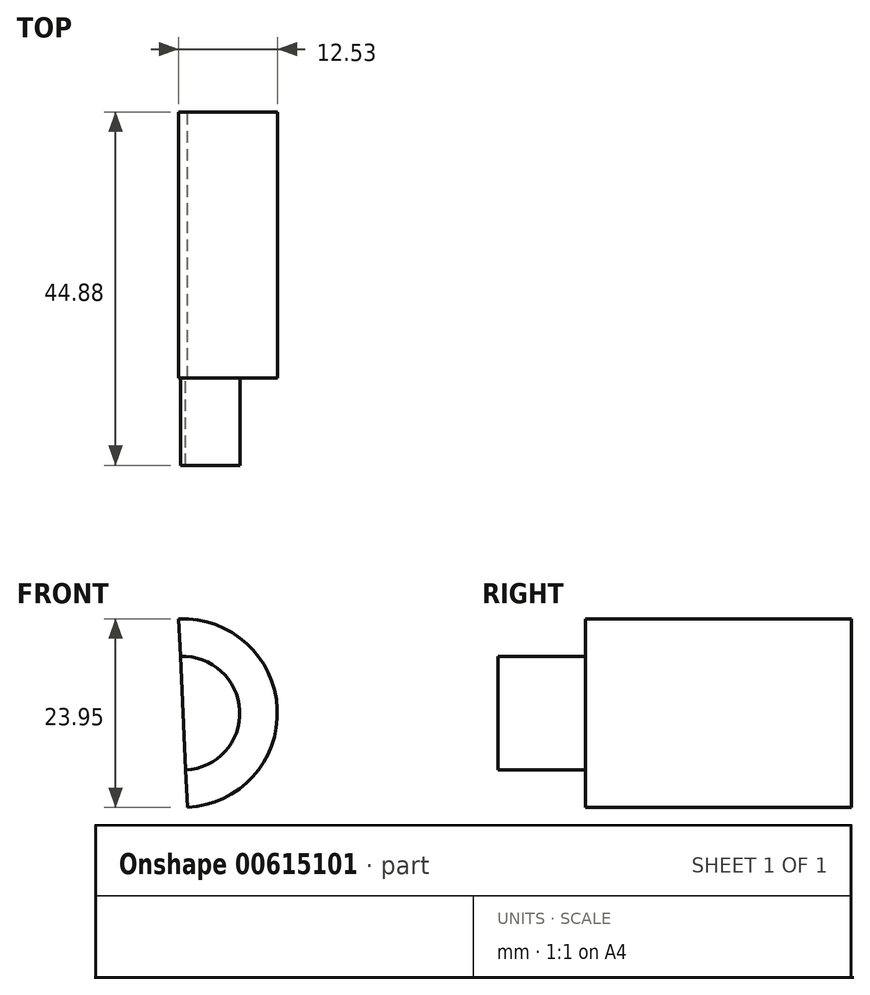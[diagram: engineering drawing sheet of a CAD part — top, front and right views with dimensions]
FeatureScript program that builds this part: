
annotation { "Feature Type Name" : "Feature", "Feature Type Description" : "" }
export const myFeature = defineFeature(function(context is Context, id is Id, definition is map)
    precondition{}
    {
        {
            var Q0;
            Q0=qCreatedBy(makeId("Front.planeOp"),FACE);
            var sketch = newSketch(context, id + "F0", { "sketchPlane" : qUnion([Q0])});
            skArc(sketch, "E0", {"start": v(-59.33, 43.04) * mm, "mid": v(-47.9, 55.56) * mm, "end": v(-60.43, 66.98) * mm});
            skLineSegment(sketch, "E1", {"start": v(-60.43, 66.98) * mm, "end": v(-59.33, 43.04) * mm});
            skSolve(sketch);
        }
        {
            var Q0;
            Q0 = qSketchRegion(id + "F0", true);
            extrude(context, id + "F1", {"entities" : qUnion([Q0]), "depth" : 33.78 * mm, "offsetDistance" : 25.4 * mm});
        }
        {
            var Q0;
            Q0=makeQuery(id+"F1.opExtrude","CAP_FACE",FACE,{"disambiguationData":[OSD([sQuery(id+"F0.wireOp",EDGE,"E0"),sQuery(id+"F0.wireOp",EDGE,"E1")])],"isStart":false});
            var sketch = newSketch(context, id + "F2", { "sketchPlane" : qUnion([Q0])});
            skArc(sketch, "E2", {"start": v(-59.54, 47.8) * mm, "mid": v(-52.67, 55.34) * mm, "end": v(-60.2, 62.21) * mm});
            skLineSegment(sketch, "E3", {"start": v(-60.2, 62.21) * mm, "end": v(-59.54, 47.8) * mm});
            skSolve(sketch);
        }
        {
            var Q0;
            Q0 = qSketchRegion(id + "F2", true);
            extrude(context, id + "F3", {"entities" : qUnion([Q0]), "operationType" : NewBodyOperationType.ADD, "depth" : 11.1 * mm, "offsetDistance" : 25.4 * mm});
        }
    });
